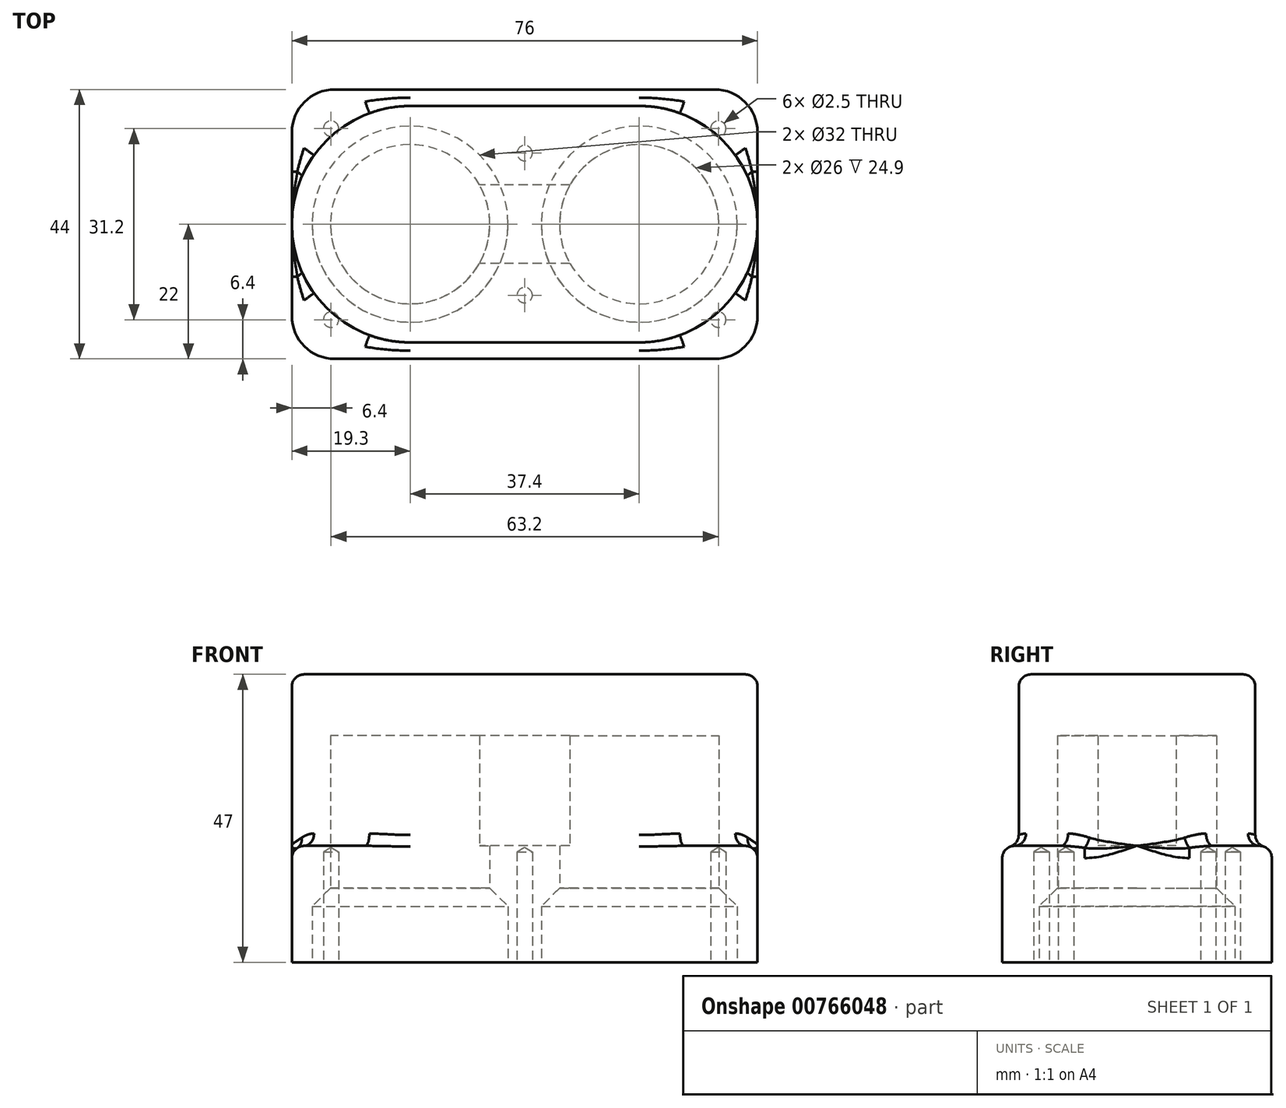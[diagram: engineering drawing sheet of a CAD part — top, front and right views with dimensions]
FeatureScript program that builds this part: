
annotation { "Feature Type Name" : "Feature", "Feature Type Description" : "" }
export const myFeature = defineFeature(function(context is Context, id is Id, definition is map)
    precondition{}
    {
        {
            var Q0;
            Q0=qCreatedBy(makeId("Top.planeOp"),FACE);
            var sketch = newSketch(context, id + "F0", { "sketchPlane" : qUnion([Q0])});
            skLineSegment(sketch, "E0.bottom", {"start": v(0, 0) * mm, "end": v(76, 0) * mm});
            skLineSegment(sketch, "E0.top", {"start": v(0, 44) * mm, "end": v(76, 44) * mm});
            skLineSegment(sketch, "E0.left", {"start": v(0, 0) * mm, "end": v(0, 44) * mm});
            skLineSegment(sketch, "E0.right", {"start": v(76, 0) * mm, "end": v(76, 44) * mm});
            skLineSegment(sketch, "E1", {"start": v(0, 22) * mm, "end": v(76, 22) * mm, "construction": true});
            skLineSegment(sketch, "E2", {"start": v(0, 22) * mm, "end": v(19.3, 22) * mm, "construction": true});
            skCircle(sketch, "E3", {"center": v(19.3, 22) * mm, "radius": 16 * mm});
            skLineSegment(sketch, "E4", {"start": v(38, 44) * mm, "end": v(38, 53.28) * mm, "construction": true});
            skCircle(sketch, "E5.MirrorC", {"center": v(56.7, 22) * mm, "radius": 16 * mm});
            skSolve(sketch);
        }
        {
            var Q0;
            Q0 = qSketchRegion(id + "F0", true);
            extrude(context, id + "F1", {"entities" : qUnion([Q0]), "depth" : 7 * mm, "offsetDistance" : 25 * mm});
        }
        {
            var Q0;
            Q0=makeQuery(id+"F1.opExtrude","CAP_FACE",FACE,{"disambiguationData":[OSD([sQuery(id+"F0.wireOp",EDGE,"E0.bottom"),sQuery(id+"F0.wireOp",EDGE,"E0.top"),sQuery(id+"F0.wireOp",EDGE,"E0.left"),sQuery(id+"F0.wireOp",EDGE,"E0.right"),sQuery(id+"F0.wireOp",EDGE,"E3"),sQuery(id+"F0.wireOp",EDGE,"E5.MirrorC")])],"isStart":false});
            var sketch = newSketch(context, id + "F2", { "sketchPlane" : qUnion([Q0])});
            skLineSegment(sketch, "E6.bottom", {"start": v(0, 44) * mm, "end": v(76, 44) * mm});
            skLineSegment(sketch, "E6.top", {"start": v(0, 0) * mm, "end": v(76, 0) * mm});
            skLineSegment(sketch, "E6.left", {"start": v(0, 44) * mm, "end": v(0, 0) * mm});
            skLineSegment(sketch, "E6.right", {"start": v(76, 44) * mm, "end": v(76, 0) * mm});
            skCircle(sketch, "E7", {"center": v(19.3, 22) * mm, "radius": 13 * mm});
            skCircle(sketch, "E8.MirrorC", {"center": v(56.7, 22) * mm, "radius": 13 * mm});
            skSolve(sketch);
        }
        {
            var Q0;
            Q0 = qSketchRegion(id + "F2", true);
            extrude(context, id + "F3", {"entities" : qUnion([Q0]), "operationType" : NewBodyOperationType.ADD, "depth" : 12 * mm, "offsetDistance" : 25 * mm});
        }
        {
            var Q0;
            Q0=makeQuery(id+"F3.opExtrude","CAP_FACE",FACE,{"disambiguationData":[OSD([sQuery(id+"F2.wireOp",EDGE,"E6.bottom"),sQuery(id+"F2.wireOp",EDGE,"E6.top"),sQuery(id+"F2.wireOp",EDGE,"E6.left"),sQuery(id+"F2.wireOp",EDGE,"E6.right"),sQuery(id+"F2.wireOp",EDGE,"E7"),sQuery(id+"F2.wireOp",EDGE,"E8.MirrorC")])],"isStart":false});
            var sketch = newSketch(context, id + "F4", { "sketchPlane" : qUnion([Q0])});
            skArc(sketch, "E9", {"start": v(19.3, 41.3) * mm, "mid": v(0, 22) * mm, "end": v(19.3, 2.7) * mm});
            skArc(sketch, "E10", {"start": v(56.7, 2.7) * mm, "mid": v(76, 22) * mm, "end": v(56.7, 41.3) * mm});
            skLineSegment(sketch, "E11", {"start": v(56.7, 22) * mm, "end": v(56.7, 28.4) * mm, "construction": true});
            skPoint(sketch, "E12.orphan", {"position": v(38, 26.77) * mm});
            skPoint(sketch, "E13.orphan", {"position": v(38, 17.23) * mm});
            skArc(sketch, "E14.0", {"start": v(30.62, 28.4) * mm, "mid": v(6.3, 22) * mm, "end": v(30.62, 15.6) * mm});
            skArc(sketch, "E15", {"start": v(45.38, 15.6) * mm, "mid": v(69.7, 22) * mm, "end": v(45.38, 28.4) * mm});
            skLineSegment(sketch, "E16", {"start": v(19.3, 41.3) * mm, "end": v(56.7, 41.3) * mm});
            skLineSegment(sketch, "E17.MirrorCS", {"start": v(19.3, 2.7) * mm, "end": v(56.7, 2.7) * mm});
            skPoint(sketch, "E18.end.orphan", {"position": v(37.5, 28.4) * mm});
            skPoint(sketch, "E19.orphan", {"position": v(38.5, 28.4) * mm});
            skPoint(sketch, "E20.MirrorCS.start.orphan", {"position": v(38.5, 15.6) * mm});
            skPoint(sketch, "E21.orphan", {"position": v(37.5, 15.6) * mm});
            skLineSegment(sketch, "E22", {"start": v(45.38, 28.4) * mm, "end": v(30.62, 28.4) * mm});
            skLineSegment(sketch, "E23.MirrorCS", {"start": v(45.38, 15.6) * mm, "end": v(30.62, 15.6) * mm});
            skSolve(sketch);
        }
        {
            var Q0;
            Q0 = qSketchRegion(id + "F4", true);
            extrude(context, id + "F5", {"entities" : qUnion([Q0]), "operationType" : NewBodyOperationType.ADD, "depth" : 18 * mm, "offsetDistance" : 25 * mm});
        }
        {
            var Q0;
            Q0 = qSketchRegion(id + "F4", true);
            extrude(context, id + "F6", {"entities" : qUnion([Q0]), "operationType" : NewBodyOperationType.ADD, "depth" : 15 * mm, "offsetDistance" : 25 * mm});
        }
        {
            var Q0;
            Q0=makeQuery(id+"F5.opExtrude","CAP_FACE",FACE,{"disambiguationData":[OSD([sQuery(id+"F4.wireOp",EDGE,"E9"),sQuery(id+"F4.wireOp",EDGE,"E10"),sQuery(id+"F4.wireOp",EDGE,"E14.0"),sQuery(id+"F4.wireOp",EDGE,"E15"),sQuery(id+"F4.wireOp",EDGE,"E16"),sQuery(id+"F4.wireOp",EDGE,"E17.MirrorCS"),sQuery(id+"F4.wireOp",EDGE,"E22"),sQuery(id+"F4.wireOp",EDGE,"E23.MirrorCS")])],"isStart":false});
            var sketch = newSketch(context, id + "F7", { "sketchPlane" : qUnion([Q0])});
            skArc(sketch, "E24", {"start": v(19.3, 41.3) * mm, "mid": v(0, 22) * mm, "end": v(19.3, 2.7) * mm});
            skArc(sketch, "E25", {"start": v(56.7, 41.3) * mm, "mid": v(76, 22) * mm, "end": v(56.7, 2.7) * mm});
            skLineSegment(sketch, "E26", {"start": v(56.7, 41.3) * mm, "end": v(19.3, 41.3) * mm});
            skLineSegment(sketch, "E27", {"start": v(56.7, 2.7) * mm, "end": v(19.3, 2.7) * mm});
            skSolve(sketch);
        }
        {
            var Q0;
            Q0 = qSketchRegion(id + "F7", true);
            extrude(context, id + "F8", {"entities" : qUnion([Q0]), "operationType" : NewBodyOperationType.ADD, "depth" : 10 * mm, "offsetDistance" : 25 * mm});
        }
        {
            var Q0;
            Q0=makeQuery(id+"F3.opExtrude","CAP_EDGE",EDGE,{"disambiguationData":[OSD([sQuery(id+"F2.wireOp",EDGE,"E7")])],"isStart":true});
            var Q1;
            Q1=makeQuery(id+"F3.opExtrude","CAP_EDGE",EDGE,{"disambiguationData":[OSD([sQuery(id+"F2.wireOp",EDGE,"E8.MirrorC")])],"isStart":true});
            chamfer(context, id + "F9", {"entities" : qUnion([Q0, Q1]), "width" : 5.1 * mm, "tangentPropagation" : true});
        }
        {
            var Q0;
            Q0=makeQuery(id+"F0.imprint","IMPRINT",FACE,{"disambiguationData":[TD([[makeQuery(id+"F0.imprint","IMPRINT",EDGE,{"derivedFrom":sQuery(id+"F0.wireOp",EDGE,"E0.bottom")}),1.0]])]});
            var sketch = newSketch(context, id + "F10", { "sketchPlane" : qUnion([Q0])});
            skLineSegment(sketch, "E28", {"start": v(38, 0) * mm, "end": v(38, 10.4) * mm, "construction": true});
            skLineSegment(sketch, "E29.MirrorCS", {"start": v(38, 44) * mm, "end": v(38, 33.6) * mm, "construction": true});
            skLineSegment(sketch, "E30", {"start": v(6.4, 0) * mm, "end": v(6.4, 6.4) * mm, "construction": true});
            skLineSegment(sketch, "E31", {"start": v(6.4, 0) * mm, "end": v(0, 0) * mm, "construction": true});
            skLineSegment(sketch, "E32.MirrorCS", {"start": v(6.4, 44) * mm, "end": v(6.4, 37.6) * mm, "construction": true});
            skLineSegment(sketch, "E33.MirrorCS", {"start": v(69.6, 0) * mm, "end": v(69.6, 6.4) * mm, "construction": true});
            skLineSegment(sketch, "E34.MirrorCS", {"start": v(69.6, 44) * mm, "end": v(69.6, 37.6) * mm, "construction": true});
            skSolve(sketch);
        }
        {
            var Q0;
            Q0=sQuery(id+"F10.wireOp",VERTEX,"E30.end");
            var Q1;
            Q1=sQuery(id+"F10.wireOp",VERTEX,"E32.MirrorCS.end");
            var Q2;
            Q2=sQuery(id+"F10.wireOp",VERTEX,"E29.MirrorCS.end");
            var Q3;
            Q3=sQuery(id+"F10.wireOp",VERTEX,"E28.end");
            var Q4;
            Q4=sQuery(id+"F10.wireOp",VERTEX,"E33.MirrorCS.end");
            var Q5;
            Q5=sQuery(id+"F10.wireOp",VERTEX,"E34.MirrorCS.end");
            var Q6;
            Q6=makeQuery(id+"F1.opExtrude","SWEPT_BODY",BODY,{"disambiguationData":[OSD([sQuery(id+"F0.wireOp",EDGE,"E0.bottom"),sQuery(id+"F0.wireOp",EDGE,"E0.top"),sQuery(id+"F0.wireOp",EDGE,"E0.left"),sQuery(id+"F0.wireOp",EDGE,"E0.right"),sQuery(id+"F0.wireOp",EDGE,"E3"),sQuery(id+"F0.wireOp",EDGE,"E5.MirrorC")])]});
            hole(context, id + "F11", {"style" : HoleStyle.SIMPLE, "endStyle" : HoleEndStyle.BLIND, "oppositeDirection" : true, "holeDiameter" : 2.5 * mm, "majorDiameter" : 5 * mm, "holeDepth" : 18 * mm, "isTappedThrough" : true, "tappedDepth" : 12 * mm, "tapClearance" : 3, "locations" : qUnion([Q0, Q1, Q2, Q3, Q4, Q5]), "scope" : qUnion([Q6])});
        }
        {
            var Q0;
            Q0=makeQuery(id+"F3.boolean.opBoolean","MERGE",EDGE,{"derivedFrom":[makeQuery(id+"F1.opExtrude","SWEPT_EDGE",EDGE,{"disambiguationData":[OSD([sQuery(id+"F0.wireOp",EDGE,"E0.bottom"),sQuery(id+"F0.wireOp",EDGE,"E0.left")])]}),makeQuery(id+"F3.opExtrude","SWEPT_EDGE",EDGE,{"disambiguationData":[OSD([sQuery(id+"F2.wireOp",EDGE,"E6.top"),sQuery(id+"F2.wireOp",EDGE,"E6.left")])]})]});
            var Q1;
            Q1=makeQuery(id+"F3.boolean.opBoolean","MERGE",EDGE,{"derivedFrom":[makeQuery(id+"F1.opExtrude","SWEPT_EDGE",EDGE,{"disambiguationData":[OSD([sQuery(id+"F0.wireOp",EDGE,"E0.top"),sQuery(id+"F0.wireOp",EDGE,"E0.left")])]}),makeQuery(id+"F3.opExtrude","SWEPT_EDGE",EDGE,{"disambiguationData":[OSD([sQuery(id+"F2.wireOp",EDGE,"E6.bottom"),sQuery(id+"F2.wireOp",EDGE,"E6.left")])]})]});
            var Q2;
            Q2=makeQuery(id+"F3.boolean.opBoolean","MERGE",EDGE,{"derivedFrom":[makeQuery(id+"F1.opExtrude","SWEPT_EDGE",EDGE,{"disambiguationData":[OSD([sQuery(id+"F0.wireOp",EDGE,"E0.top"),sQuery(id+"F0.wireOp",EDGE,"E0.right")])]}),makeQuery(id+"F3.opExtrude","SWEPT_EDGE",EDGE,{"disambiguationData":[OSD([sQuery(id+"F2.wireOp",EDGE,"E6.bottom"),sQuery(id+"F2.wireOp",EDGE,"E6.right")])]})]});
            var Q3;
            Q3=makeQuery(id+"F3.boolean.opBoolean","MERGE",EDGE,{"derivedFrom":[makeQuery(id+"F1.opExtrude","SWEPT_EDGE",EDGE,{"disambiguationData":[OSD([sQuery(id+"F0.wireOp",EDGE,"E0.bottom"),sQuery(id+"F0.wireOp",EDGE,"E0.right")])]}),makeQuery(id+"F3.opExtrude","SWEPT_EDGE",EDGE,{"disambiguationData":[OSD([sQuery(id+"F2.wireOp",EDGE,"E6.top"),sQuery(id+"F2.wireOp",EDGE,"E6.right")])]})]});
            fillet(context, id + "F12", {"entities" : qUnion([Q0, Q1, Q2, Q3]), "radius" : 7 * mm, "tangentPropagation" : true, "allowEdgeOverflow" : false});
        }
        {
            var Q0;
            Q0=makeQuery(id+"F3.opExtrude","CAP_EDGE",EDGE,{"disambiguationData":[OSD([sQuery(id+"F2.wireOp",EDGE,"E6.bottom")])],"isStart":false});
            var Q1;
            Q1=makeQuery(id+"F8.opExtrude","CAP_EDGE",EDGE,{"disambiguationData":[OSD([sQuery(id+"F7.wireOp",EDGE,"E27")])],"isStart":false});
            fillet(context, id + "F13", {"entities" : qUnion([Q0, Q1]), "radius" : 2 * mm, "tangentPropagation" : true, "allowEdgeOverflow" : false});
        }
        {
            var Q0;
            {var subQ0=sQuery(id+"F4.wireOp",EDGE,"E9");Q0=makeQuery(id+"F5.boolean.opBoolean","SPLIT",EDGE,{"disambiguationData":[TD([makeQuery(id+"F5.opExtrude","SWEPT_FACE",FACE,{"disambiguationData":[OSD([sQuery(id+"F4.wireOp",EDGE,"E16")])]})])],"derivedFrom":makeQuery(id+"F5.opExtrude","CAP_EDGE",EDGE,{"disambiguationData":[OSD([subQ0])],"isStart":true})});}
            var Q1;
            {var subQ0=sQuery(id+"F4.wireOp",EDGE,"E9");Q1=makeQuery(id+"F5.boolean.opBoolean","SPLIT",EDGE,{"disambiguationData":[TD([makeQuery(id+"F5.opExtrude","SWEPT_FACE",FACE,{"disambiguationData":[OSD([sQuery(id+"F4.wireOp",EDGE,"E17.MirrorCS")])]})])],"derivedFrom":makeQuery(id+"F5.opExtrude","CAP_EDGE",EDGE,{"disambiguationData":[OSD([subQ0])],"isStart":true})});}
            fillet(context, id + "F14", {"entities" : qUnion([Q0, Q1]), "radius" : 2 * mm, "tangentPropagation" : true, "allowEdgeOverflow" : false});
        }
    });
